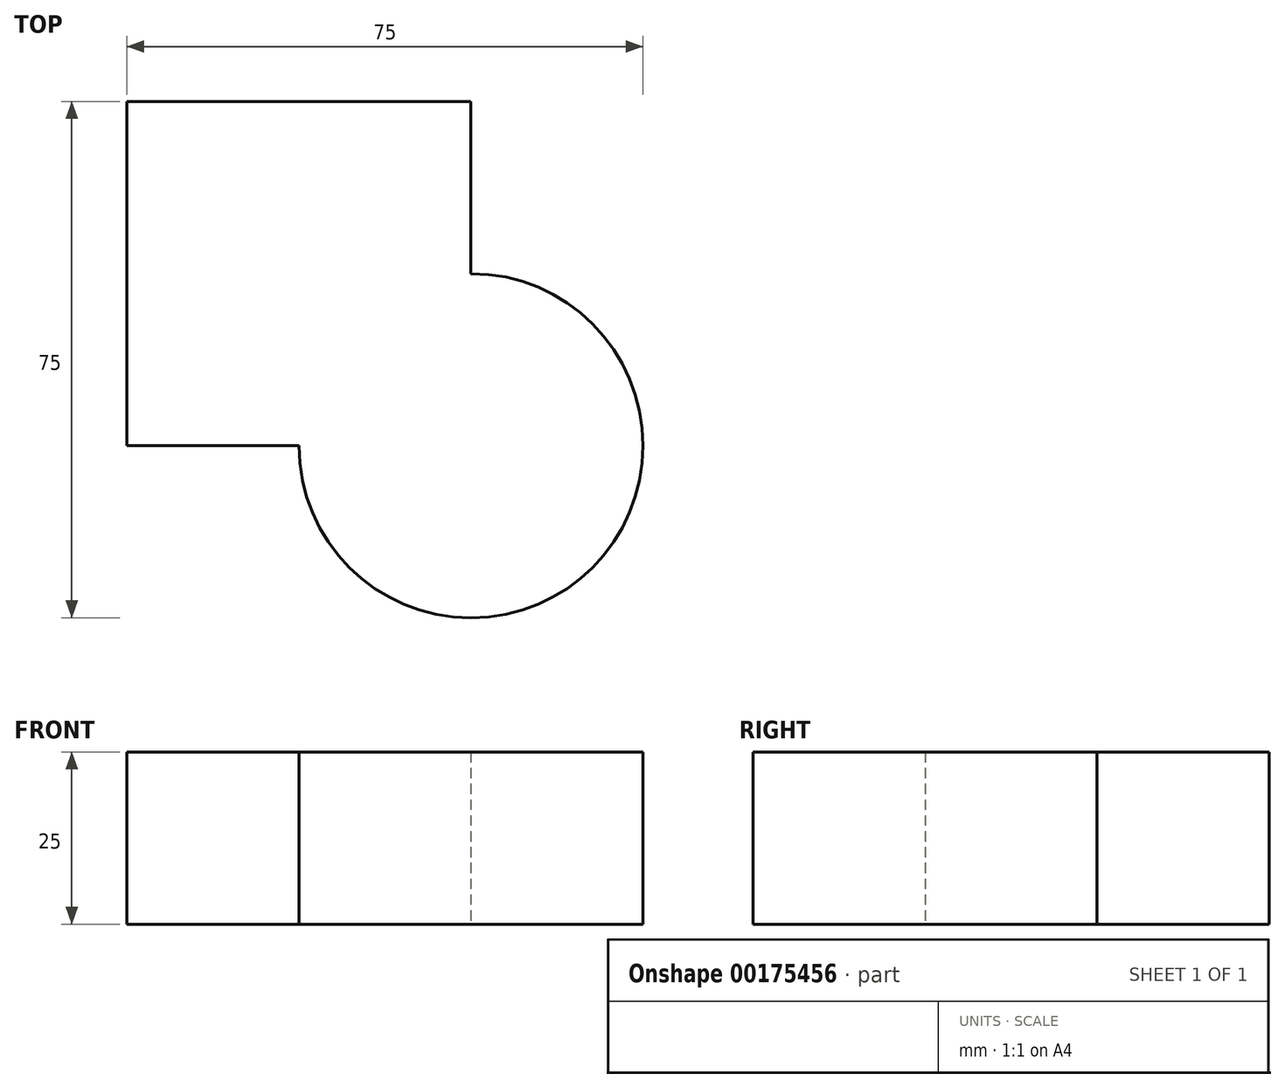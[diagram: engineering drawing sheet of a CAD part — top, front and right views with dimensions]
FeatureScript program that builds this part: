
annotation { "Feature Type Name" : "Feature", "Feature Type Description" : "" }
export const myFeature = defineFeature(function(context is Context, id is Id, definition is map)
    precondition{}
    {
        {
            var Q0;
            Q0=qCreatedBy(makeId("Top.planeOp"),FACE);
            var sketch = newSketch(context, id + "F0", { "sketchPlane" : qUnion([Q0])});
            skLineSegment(sketch, "E0.bottom", {"start": v(-35.87, 46.93) * mm, "end": v(14.13, 46.93) * mm});
            skLineSegment(sketch, "E0.top", {"start": v(-35.87, -3.07) * mm, "end": v(14.13, -3.07) * mm});
            skLineSegment(sketch, "E0.left", {"start": v(-35.87, 46.93) * mm, "end": v(-35.87, -3.07) * mm});
            skLineSegment(sketch, "E0.right", {"start": v(14.13, 46.93) * mm, "end": v(14.13, -3.07) * mm});
            skCircle(sketch, "E1", {"center": v(14.13, -3.07) * mm, "radius": 25 * mm});
            skSolve(sketch);
        }
        {
            var Q0;
            {var subQ0=sQuery(id+"F0.wireOp",EDGE,"E0.right");var subQ1=sQuery(id+"F0.wireOp",EDGE,"E0.top");var subQ2=makeQuery(id+"F0.imprint","INTERSECT",VERTEX,{"derivedFrom":[subQ1,subQ0]});Q0=makeQuery(id+"F0.imprint","IMPRINT",FACE,{"disambiguationData":[TD([[makeQuery(id+"F0.imprint","IMPRINT",EDGE,{"disambiguationData":[TD([[subQ2,1.0]])],"derivedFrom":subQ1}),-1.0]])]});}
            var Q1;
            {var subQ0=sQuery(id+"F0.wireOp",EDGE,"E0.right");var subQ1=sQuery(id+"F0.wireOp",EDGE,"E0.top");var subQ2=makeQuery(id+"F0.imprint","INTERSECT",VERTEX,{"derivedFrom":[subQ1,subQ0]});Q1=makeQuery(id+"F0.imprint","IMPRINT",FACE,{"disambiguationData":[TD([[makeQuery(id+"F0.imprint","IMPRINT",EDGE,{"disambiguationData":[TD([[subQ2,1.0]])],"derivedFrom":subQ1}),1.0]])]});}
            var Q2;
            {var subQ1=sQuery(id+"F0.wireOp",EDGE,"E0.bottom");Q2=makeQuery(id+"F0.imprint","IMPRINT",FACE,{"disambiguationData":[TD([[makeQuery(id+"F0.imprint","IMPRINT",EDGE,{"derivedFrom":subQ1}),-1.0]])]});}
            extrude(context, id + "F1", {"entities" : qUnion([Q0, Q1, Q2]), "depth" : 25 * mm});
        }
    });
